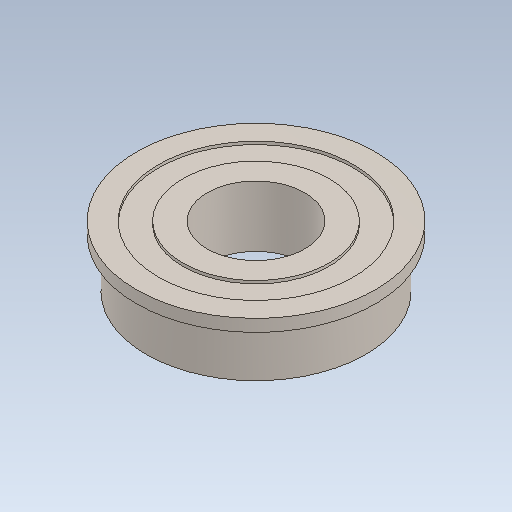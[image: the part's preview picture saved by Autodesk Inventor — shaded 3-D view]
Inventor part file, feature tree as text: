
AUTODESK INVENTOR PART (.ipt)
format: ipt  version: 2020 (Build 240168000, 168)  size: 111,104 bytes
history: native  units: in
note: dims shown in document units (in); Inventor stores cm internally (conversion verified against a paired STEP export)
features: revolve x1
ambient origin geometry x8: Origin, YZ Plane, XZ Plane, XY Plane, X Axis, Y Axis, Z Axis, Center Point
bodies: Solid1 (feature_tree)
feature tree (1):
  revolve  "Revolve1"  [1 undecoded]
note: 1 required parameter value undecoded (feature->parameter linkage not recoverable at this tier; creation-order binding heuristic only, values carry confidence <= 0.55)
